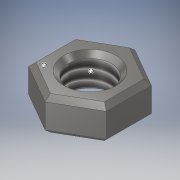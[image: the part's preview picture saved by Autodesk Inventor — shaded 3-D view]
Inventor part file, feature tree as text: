
AUTODESK INVENTOR PART (.ipt)
format: ipt  version: 2018 (Build 220112000, 112)  size: 137,216 bytes
history: native  units: in
note: dims shown in document units (in); Inventor stores cm internally (conversion verified against a paired STEP export)
features: extrude x2, sketch x2, chamfer x1, thread x1
ambient origin geometry x8: Origin, YZ Plane, XZ Plane, XY Plane, X Axis, Y Axis, Z Axis, Center Point
bodies: Solid1 (feature_tree)
feature tree (6):
  extrude  "Extrusion1"  Depth=0.108in TaperAngle=0.0deg
  extrude  "Extrusion2"  Depth=0.108in TaperAngle=0.0deg
  chamfer  "Chamfer1"  Distance=0.015in Angle=45.0deg
  thread  "Thread1"  [1 undecoded]
  sketch  "Sketch1"  dims[d0=0.25in d1=0.108in d2=0.0in]
  sketch  "Sketch2"  dims[d3=0.138in d4=0.108in d5=0.0in d6=0.015in d7=0.125in d8=45.0deg d9=1.0in d10=0.0in d12=0.0in d13=0.0in]
note: 1 required parameter value undecoded (feature->parameter linkage not recoverable at this tier; creation-order binding heuristic only, values carry confidence <= 0.55)
